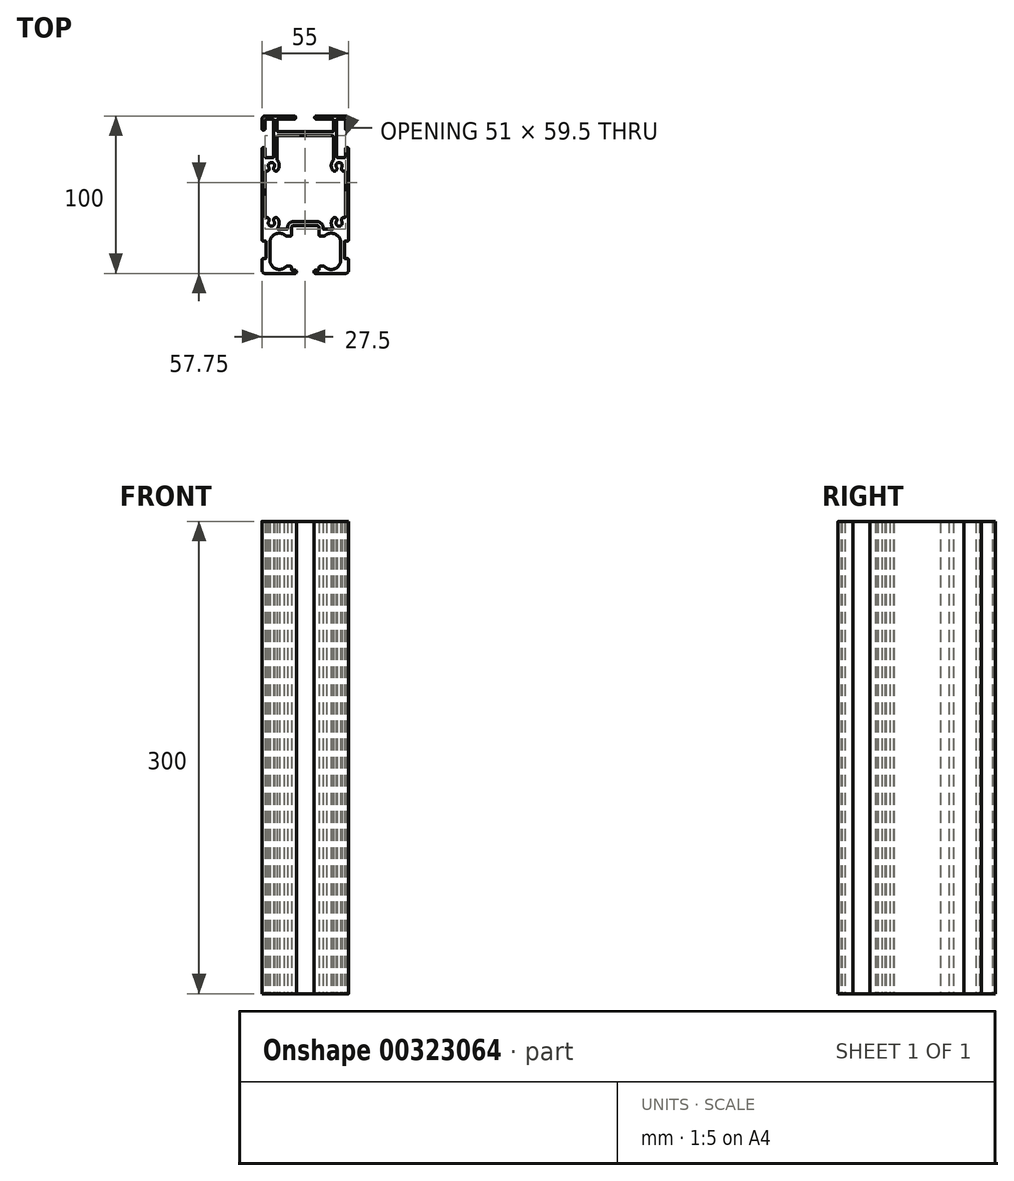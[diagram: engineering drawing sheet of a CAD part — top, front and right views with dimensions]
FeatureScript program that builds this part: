
annotation { "Feature Type Name" : "Feature", "Feature Type Description" : "" }
export const myFeature = defineFeature(function(context is Context, id is Id, definition is map)
    precondition{}
    {
        {
            var Q0;
            Q0=qCreatedBy(makeId("Top.planeOp"),FACE);
            var sketch = newSketch(context, id + "F0", { "sketchPlane" : qUnion([Q0])});
            skArc(sketch, "E0.0.0", {"start": v(6.5, -48) * mm, "mid": v(5.5, -49) * mm, "end": v(6.5, -50) * mm});
            skLineSegment(sketch, "E0.0.1", {"start": v(6.5, -50) * mm, "end": v(25.5, -50) * mm});
            skArc(sketch, "E0.0.2", {"start": v(25.5, -50) * mm, "mid": v(26.91, -49.41) * mm, "end": v(27.5, -48) * mm});
            skLineSegment(sketch, "E0.0.3", {"start": v(27.5, -48) * mm, "end": v(27.5, -41.5) * mm});
            skArc(sketch, "E0.0.4", {"start": v(27.5, -41.5) * mm, "mid": v(27.2, -40.8) * mm, "end": v(26.5, -40.5) * mm});
            skLineSegment(sketch, "E0.0.5", {"start": v(26.5, -40.5) * mm, "end": v(25.3, -40.5) * mm});
            skArc(sketch, "E0.0.6", {"start": v(25.3, -40.5) * mm, "mid": v(24.96, -40.35) * mm, "end": v(24.8, -40) * mm});
            skLineSegment(sketch, "E0.0.7", {"start": v(24.8, -40) * mm, "end": v(24.8, -30) * mm});
            skArc(sketch, "E0.0.8", {"start": v(24.8, -30) * mm, "mid": v(24.96, -29.65) * mm, "end": v(25.3, -29.5) * mm});
            skLineSegment(sketch, "E0.0.9", {"start": v(25.3, -29.5) * mm, "end": v(26.5, -29.5) * mm});
            skArc(sketch, "E0.0.10", {"start": v(26.5, -29.5) * mm, "mid": v(27.2, -29.2) * mm, "end": v(27.5, -28.5) * mm});
            skLineSegment(sketch, "E0.0.11", {"start": v(27.5, -28.5) * mm, "end": v(27.5, 29) * mm});
            skArc(sketch, "E0.0.12", {"start": v(27.5, 29) * mm, "mid": v(26.5, 30) * mm, "end": v(25.5, 29) * mm});
            skLineSegment(sketch, "E0.0.13", {"start": v(25.5, 29) * mm, "end": v(25.5, 24) * mm});
            skArc(sketch, "E0.0.14", {"start": v(25.5, 24) * mm, "mid": v(25.35, 23.65) * mm, "end": v(25, 23.5) * mm});
            skLineSegment(sketch, "E0.0.15", {"start": v(25, 23.5) * mm, "end": v(20.5, 23.5) * mm});
            skArc(sketch, "E0.0.16", {"start": v(20.5, 23.5) * mm, "mid": v(20.15, 23.65) * mm, "end": v(20, 24) * mm});
            skLineSegment(sketch, "E0.0.17", {"start": v(20, 24) * mm, "end": v(20, 47.5) * mm});
            skArc(sketch, "E0.0.18", {"start": v(20, 47.5) * mm, "mid": v(20.15, 47.85) * mm, "end": v(20.5, 48) * mm});
            skLineSegment(sketch, "E0.0.19", {"start": v(20.5, 48) * mm, "end": v(25, 48) * mm});
            skArc(sketch, "E0.0.20", {"start": v(25, 48) * mm, "mid": v(25.35, 47.85) * mm, "end": v(25.5, 47.5) * mm});
            skLineSegment(sketch, "E0.0.21", {"start": v(25.5, 47.5) * mm, "end": v(25.5, 42) * mm});
            skArc(sketch, "E0.0.22", {"start": v(25.5, 42) * mm, "mid": v(26.5, 41) * mm, "end": v(27.5, 42) * mm});
            skLineSegment(sketch, "E0.0.23", {"start": v(27.5, 42) * mm, "end": v(27.5, 48) * mm});
            skArc(sketch, "E0.0.24", {"start": v(27.5, 48) * mm, "mid": v(26.91, 49.41) * mm, "end": v(25.5, 50) * mm});
            skLineSegment(sketch, "E0.0.25", {"start": v(25.5, 50) * mm, "end": v(7, 50) * mm});
            skArc(sketch, "E0.0.26", {"start": v(7, 50) * mm, "mid": v(6, 49) * mm, "end": v(7, 48) * mm});
            skLineSegment(sketch, "E0.0.27", {"start": v(7, 48) * mm, "end": v(17.5, 48) * mm});
            skArc(sketch, "E0.0.28", {"start": v(17.5, 48) * mm, "mid": v(17.85, 47.85) * mm, "end": v(18, 47.5) * mm});
            skLineSegment(sketch, "E0.0.29", {"start": v(18, 47.5) * mm, "end": v(18, 40.5) * mm});
            skArc(sketch, "E0.0.30", {"start": v(18, 40.5) * mm, "mid": v(17.85, 40.15) * mm, "end": v(17.5, 40) * mm});
            skLineSegment(sketch, "E0.0.31", {"start": v(17.5, 40) * mm, "end": v(-17.5, 40) * mm});
            skArc(sketch, "E0.0.32", {"start": v(-17.5, 40) * mm, "mid": v(-17.85, 40.15) * mm, "end": v(-18, 40.5) * mm});
            skLineSegment(sketch, "E0.0.33", {"start": v(-18, 40.5) * mm, "end": v(-18, 47.5) * mm});
            skArc(sketch, "E0.0.34", {"start": v(-18, 47.5) * mm, "mid": v(-17.85, 47.85) * mm, "end": v(-17.5, 48) * mm});
            skLineSegment(sketch, "E0.0.35", {"start": v(-17.5, 48) * mm, "end": v(-7, 48) * mm});
            skArc(sketch, "E0.0.36", {"start": v(-7, 48) * mm, "mid": v(-6, 49) * mm, "end": v(-7, 50) * mm});
            skLineSegment(sketch, "E0.0.37", {"start": v(-7, 50) * mm, "end": v(-25.5, 50) * mm});
            skArc(sketch, "E0.0.38", {"start": v(-25.5, 50) * mm, "mid": v(-26.91, 49.41) * mm, "end": v(-27.5, 48) * mm});
            skLineSegment(sketch, "E0.0.39", {"start": v(-27.5, 48) * mm, "end": v(-27.5, 42) * mm});
            skArc(sketch, "E0.0.40", {"start": v(-27.5, 42) * mm, "mid": v(-26.5, 41) * mm, "end": v(-25.5, 42) * mm});
            skLineSegment(sketch, "E0.0.41", {"start": v(-25.5, 42) * mm, "end": v(-25.5, 47.5) * mm});
            skArc(sketch, "E0.0.42", {"start": v(-25.5, 47.5) * mm, "mid": v(-25.35, 47.85) * mm, "end": v(-25, 48) * mm});
            skLineSegment(sketch, "E0.0.43", {"start": v(-25, 48) * mm, "end": v(-20.5, 48) * mm});
            skArc(sketch, "E0.0.44", {"start": v(-20.5, 48) * mm, "mid": v(-20.15, 47.85) * mm, "end": v(-20, 47.5) * mm});
            skLineSegment(sketch, "E0.0.45", {"start": v(-20, 47.5) * mm, "end": v(-20, 24) * mm});
            skArc(sketch, "E0.0.46", {"start": v(-20, 24) * mm, "mid": v(-20.15, 23.65) * mm, "end": v(-20.5, 23.5) * mm});
            skLineSegment(sketch, "E0.0.47", {"start": v(-20.5, 23.5) * mm, "end": v(-25, 23.5) * mm});
            skArc(sketch, "E0.0.48", {"start": v(-25, 23.5) * mm, "mid": v(-25.35, 23.65) * mm, "end": v(-25.5, 24) * mm});
            skLineSegment(sketch, "E0.0.49", {"start": v(-25.5, 24) * mm, "end": v(-25.5, 29) * mm});
            skArc(sketch, "E0.0.50", {"start": v(-25.5, 29) * mm, "mid": v(-26.5, 30) * mm, "end": v(-27.5, 29) * mm});
            skLineSegment(sketch, "E0.0.51", {"start": v(-27.5, 29) * mm, "end": v(-27.5, -28.5) * mm});
            skArc(sketch, "E0.0.52", {"start": v(-27.5, -28.5) * mm, "mid": v(-27.2, -29.2) * mm, "end": v(-26.5, -29.5) * mm});
            skLineSegment(sketch, "E0.0.53", {"start": v(-26.5, -29.5) * mm, "end": v(-25.3, -29.5) * mm});
            skArc(sketch, "E0.0.54", {"start": v(-25.3, -29.5) * mm, "mid": v(-24.96, -29.65) * mm, "end": v(-24.8, -30) * mm});
            skLineSegment(sketch, "E0.0.55", {"start": v(-24.8, -30) * mm, "end": v(-24.8, -40) * mm});
            skArc(sketch, "E0.0.56", {"start": v(-24.8, -40) * mm, "mid": v(-24.96, -40.35) * mm, "end": v(-25.3, -40.5) * mm});
            skLineSegment(sketch, "E0.0.57", {"start": v(-25.3, -40.5) * mm, "end": v(-26.5, -40.5) * mm});
            skArc(sketch, "E0.0.58", {"start": v(-26.5, -40.5) * mm, "mid": v(-27.2, -40.8) * mm, "end": v(-27.5, -41.5) * mm});
            skLineSegment(sketch, "E0.0.59", {"start": v(-27.5, -41.5) * mm, "end": v(-27.5, -48) * mm});
            skArc(sketch, "E0.0.60", {"start": v(-27.5, -48) * mm, "mid": v(-26.91, -49.41) * mm, "end": v(-25.5, -50) * mm});
            skLineSegment(sketch, "E0.0.61", {"start": v(-25.5, -50) * mm, "end": v(-6.5, -50) * mm});
            skArc(sketch, "E0.0.62", {"start": v(-6.5, -50) * mm, "mid": v(-5.5, -49) * mm, "end": v(-6.5, -48) * mm});
            skLineSegment(sketch, "E0.0.63", {"start": v(-6.5, -48) * mm, "end": v(-8.34, -48) * mm});
            skArc(sketch, "E0.0.64", {"start": v(-8.34, -48) * mm, "mid": v(-8.7, -47.85) * mm, "end": v(-8.84, -47.5) * mm});
            skLineSegment(sketch, "E0.0.65", {"start": v(-8.84, -47.5) * mm, "end": v(-8.84, -46) * mm});
            skArc(sketch, "E0.0.66", {"start": v(-8.84, -46) * mm, "mid": v(-8.98, -45.65) * mm, "end": v(-9.34, -45.5) * mm});
            skLineSegment(sketch, "E0.0.67", {"start": v(-9.34, -45.5) * mm, "end": v(-11.8, -45.5) * mm});
            skArc(sketch, "E0.0.68", {"start": v(-11.8, -45.5) * mm, "mid": v(-12, -45.54) * mm, "end": v(-12.17, -45.65) * mm});
            skArc(sketch, "E0.0.69", {"start": v(-12.17, -45.65) * mm, "mid": v(-17.99, -47.31) * mm, "end": v(-22.3, -43.07) * mm});
            skArc(sketch, "E0.0.70", {"start": v(-22.3, -43.07) * mm, "mid": v(-22.3, -43) * mm, "end": v(-22.3, -42.94) * mm});
            skLineSegment(sketch, "E0.0.71", {"start": v(-22.3, -42.94) * mm, "end": v(-22.3, -29.06) * mm});
            skArc(sketch, "E0.0.72", {"start": v(-22.3, -29.06) * mm, "mid": v(-22.3, -29) * mm, "end": v(-22.3, -28.93) * mm});
            skArc(sketch, "E0.0.73", {"start": v(-22.3, -28.93) * mm, "mid": v(-18.81, -24.96) * mm, "end": v(-13.54, -25.28) * mm});
            skArc(sketch, "E0.0.74", {"start": v(-13.54, -25.28) * mm, "mid": v(-12.42, -26.04) * mm, "end": v(-11.1, -26.31) * mm});
            skLineSegment(sketch, "E0.0.75", {"start": v(-11.1, -26.31) * mm, "end": v(-9.34, -26.31) * mm});
            skArc(sketch, "E0.0.76", {"start": v(-9.34, -26.31) * mm, "mid": v(-8.98, -26.17) * mm, "end": v(-8.84, -25.81) * mm});
            skLineSegment(sketch, "E0.0.77", {"start": v(-8.84, -25.81) * mm, "end": v(-8.84, -21.1) * mm});
            skArc(sketch, "E0.0.78", {"start": v(-8.84, -21.1) * mm, "mid": v(-8.37, -19.97) * mm, "end": v(-7.24, -19.5) * mm});
            skLineSegment(sketch, "E0.0.79", {"start": v(-7.24, -19.5) * mm, "end": v(7.24, -19.5) * mm});
            skArc(sketch, "E0.0.80", {"start": v(7.24, -19.5) * mm, "mid": v(8.37, -19.97) * mm, "end": v(8.84, -21.1) * mm});
            skLineSegment(sketch, "E0.0.81", {"start": v(8.84, -21.1) * mm, "end": v(8.84, -25.81) * mm});
            skArc(sketch, "E0.0.82", {"start": v(8.84, -25.81) * mm, "mid": v(8.98, -26.17) * mm, "end": v(9.34, -26.31) * mm});
            skLineSegment(sketch, "E0.0.83", {"start": v(9.34, -26.31) * mm, "end": v(11.1, -26.31) * mm});
            skArc(sketch, "E0.0.84", {"start": v(11.1, -26.31) * mm, "mid": v(12.42, -26.04) * mm, "end": v(13.54, -25.28) * mm});
            skArc(sketch, "E0.0.85", {"start": v(13.54, -25.28) * mm, "mid": v(18.81, -24.96) * mm, "end": v(22.3, -28.93) * mm});
            skArc(sketch, "E0.0.86", {"start": v(22.3, -28.93) * mm, "mid": v(22.3, -29) * mm, "end": v(22.3, -29.06) * mm});
            skLineSegment(sketch, "E0.0.87", {"start": v(22.3, -29.06) * mm, "end": v(22.3, -42.94) * mm});
            skArc(sketch, "E0.0.88", {"start": v(22.3, -42.94) * mm, "mid": v(22.3, -43) * mm, "end": v(22.3, -43.07) * mm});
            skArc(sketch, "E0.0.89", {"start": v(22.3, -43.07) * mm, "mid": v(17.99, -47.31) * mm, "end": v(12.17, -45.65) * mm});
            skArc(sketch, "E0.0.90", {"start": v(12.17, -45.65) * mm, "mid": v(12, -45.54) * mm, "end": v(11.8, -45.5) * mm});
            skLineSegment(sketch, "E0.0.91", {"start": v(11.8, -45.5) * mm, "end": v(9.34, -45.5) * mm});
            skArc(sketch, "E0.0.92", {"start": v(9.34, -45.5) * mm, "mid": v(8.98, -45.65) * mm, "end": v(8.84, -46) * mm});
            skLineSegment(sketch, "E0.0.93", {"start": v(8.84, -46) * mm, "end": v(8.84, -47.5) * mm});
            skArc(sketch, "E0.0.94", {"start": v(8.84, -47.5) * mm, "mid": v(8.7, -47.85) * mm, "end": v(8.34, -48) * mm});
            skLineSegment(sketch, "E0.0.95", {"start": v(8.34, -48) * mm, "end": v(6.5, -48) * mm});
            skLineSegment(sketch, "E1.0", {"start": v(25.5, -14.1) * mm, "end": v(25.5, 14.6) * mm});
            skArc(sketch, "E2.0", {"start": v(24.85, 15.09) * mm, "mid": v(23.18, 15.61) * mm, "end": v(23.15, 17.36) * mm});
            skArc(sketch, "E3.0", {"start": v(25.5, 14.6) * mm, "mid": v(25.3, 15.01) * mm, "end": v(24.85, 15.09) * mm});
            skArc(sketch, "E4.0", {"start": v(23.15, 17.36) * mm, "mid": v(21.5, 20.5) * mm, "end": v(19.85, 17.36) * mm});
            skArc(sketch, "E5.0", {"start": v(19.85, 17.36) * mm, "mid": v(19.47, 15.28) * mm, "end": v(17.39, 15.66) * mm});
            skArc(sketch, "E6.0", {"start": v(17.39, 15.66) * mm, "mid": v(16.51, 18.88) * mm, "end": v(17.86, 21.93) * mm});
            skArc(sketch, "E7.0", {"start": v(17.86, 21.93) * mm, "mid": v(17.96, 22.1) * mm, "end": v(18, 22.28) * mm});
            skLineSegment(sketch, "E8.0", {"start": v(18, 22.28) * mm, "end": v(18, 36.5) * mm});
            skLineSegment(sketch, "E9.0", {"start": v(17, 37.5) * mm, "end": v(-17, 37.5) * mm});
            skArc(sketch, "E10.0", {"start": v(18, 36.5) * mm, "mid": v(17.7, 37.2) * mm, "end": v(17, 37.5) * mm});
            skArc(sketch, "E11.0", {"start": v(24.85, -14.59) * mm, "mid": v(25.3, -14.51) * mm, "end": v(25.5, -14.1) * mm});
            skArc(sketch, "E12.0", {"start": v(23.15, -16.86) * mm, "mid": v(23.18, -15.11) * mm, "end": v(24.85, -14.59) * mm});
            skArc(sketch, "E13.0", {"start": v(19.85, -16.86) * mm, "mid": v(21.5, -20) * mm, "end": v(23.15, -16.86) * mm});
            skArc(sketch, "E14.0", {"start": v(17.39, -15.16) * mm, "mid": v(19.47, -14.78) * mm, "end": v(19.85, -16.86) * mm});
            skArc(sketch, "E15.0", {"start": v(17.64, -21.18) * mm, "mid": v(16.5, -18.21) * mm, "end": v(17.39, -15.16) * mm});
            skArc(sketch, "E16.0", {"start": v(17.26, -22) * mm, "mid": v(17.7, -21.71) * mm, "end": v(17.64, -21.18) * mm});
            skLineSegment(sketch, "E17.0", {"start": v(11.84, -22) * mm, "end": v(17.26, -22) * mm});
            skArc(sketch, "E18.0", {"start": v(11.34, -21.5) * mm, "mid": v(11.48, -21.85) * mm, "end": v(11.84, -22) * mm});
            skLineSegment(sketch, "E19.0", {"start": v(11.34, -21.1) * mm, "end": v(11.34, -21.5) * mm});
            skArc(sketch, "E20.0", {"start": v(7.24, -17) * mm, "mid": v(10.14, -18.2) * mm, "end": v(11.34, -21.1) * mm});
            skLineSegment(sketch, "E21.0", {"start": v(-7.24, -17) * mm, "end": v(7.24, -17) * mm});
            skArc(sketch, "E22.0", {"start": v(-11.34, -21.1) * mm, "mid": v(-10.14, -18.2) * mm, "end": v(-7.24, -17) * mm});
            skLineSegment(sketch, "E23.0", {"start": v(-11.34, -21.5) * mm, "end": v(-11.34, -21.1) * mm});
            skArc(sketch, "E24.0", {"start": v(-11.84, -22) * mm, "mid": v(-11.48, -21.85) * mm, "end": v(-11.34, -21.5) * mm});
            skLineSegment(sketch, "E25.0", {"start": v(-17.26, -22) * mm, "end": v(-11.84, -22) * mm});
            skArc(sketch, "E26.0", {"start": v(-17.64, -21.18) * mm, "mid": v(-17.7, -21.71) * mm, "end": v(-17.26, -22) * mm});
            skArc(sketch, "E27.0", {"start": v(-17.39, -15.16) * mm, "mid": v(-16.5, -18.21) * mm, "end": v(-17.64, -21.18) * mm});
            skArc(sketch, "E28.0", {"start": v(-19.85, -16.86) * mm, "mid": v(-19.47, -14.78) * mm, "end": v(-17.39, -15.16) * mm});
            skArc(sketch, "E29.0", {"start": v(-23.15, -16.86) * mm, "mid": v(-21.5, -20) * mm, "end": v(-19.85, -16.86) * mm});
            skArc(sketch, "E30.0", {"start": v(-24.85, -14.59) * mm, "mid": v(-23.18, -15.11) * mm, "end": v(-23.15, -16.86) * mm});
            skArc(sketch, "E31.0", {"start": v(-25.5, -14.1) * mm, "mid": v(-25.3, -14.51) * mm, "end": v(-24.85, -14.59) * mm});
            skLineSegment(sketch, "E32.0", {"start": v(-25.5, 14.6) * mm, "end": v(-25.5, -14.1) * mm});
            skArc(sketch, "E33.0", {"start": v(-24.85, 15.09) * mm, "mid": v(-25.3, 15.01) * mm, "end": v(-25.5, 14.6) * mm});
            skArc(sketch, "E34.0", {"start": v(-23.15, 17.36) * mm, "mid": v(-23.18, 15.61) * mm, "end": v(-24.85, 15.09) * mm});
            skArc(sketch, "E35.0", {"start": v(-19.85, 17.36) * mm, "mid": v(-21.5, 20.5) * mm, "end": v(-23.15, 17.36) * mm});
            skArc(sketch, "E36.0", {"start": v(-17.39, 15.66) * mm, "mid": v(-19.47, 15.28) * mm, "end": v(-19.85, 17.36) * mm});
            skArc(sketch, "E37.0", {"start": v(-17.86, 21.93) * mm, "mid": v(-16.51, 18.88) * mm, "end": v(-17.39, 15.66) * mm});
            skArc(sketch, "E38.0", {"start": v(-18, 22.28) * mm, "mid": v(-17.96, 22.1) * mm, "end": v(-17.86, 21.93) * mm});
            skLineSegment(sketch, "E39.0", {"start": v(-18, 36.5) * mm, "end": v(-18, 22.28) * mm});
            skArc(sketch, "E40.0", {"start": v(-17, 37.5) * mm, "mid": v(-17.7, 37.2) * mm, "end": v(-18, 36.5) * mm});
            skLineSegment(sketch, "E41", {"start": v(-7, 50) * mm, "end": v(7, 50) * mm, "construction": true});
            skLineSegment(sketch, "E42", {"start": v(-6.5, -50) * mm, "end": v(6.5, -50) * mm, "construction": true});
            skLineSegment(sketch, "E43", {"start": v(0, -50) * mm, "end": v(0, 50) * mm, "construction": true});
            skLineSegment(sketch, "E44", {"start": v(38.39, 0) * mm, "end": v(-38.32, 0) * mm, "construction": true});
            skPoint(sketch, "E44.startSnap0", {"position": v(0, 0) * mm});
            skSolve(sketch);
        }
        {
            var Q0;
            Q0 = qSketchRegion(id + "F0", true);
            extrude(context, id + "F1", {"entities" : qUnion([Q0]), "endBound" : BoundingType.SYMMETRIC, "depth" : 300 * mm});
        }
    });
